# Revit family: IS_iLifeS_E2539_BIM_GB
name_source: partatom
category: Plumbing Fixtures
units: mm (PartAtom-declared; Revit-internal decimal feet)

## family parameters
Always vertical = No
Cut with Voids When Loaded = No
OmniClass Number = 23.45.05.14.14
OmniClass Title = Sinks/Lavatories
Part Type = Normal
Room Calculation Point = No
Round Connector Dimension = Use Diameter
Shared = No
Work Plane-Based = No

## types (1)
- E253901 - i.life S pedestal - White
    Accessories = https://www.idealstandard.co.uk
    AreaUnits = millimetres
    AssetType = Fixed
    BIMObjectName = IS_IdealStandard_Pedestal washbasins_i.lifeS_E2539
    BIMobject category = Wash Basins
    BIMobject category code = wash-basins
    BIMobject main category = Sanitary
    BIMobject main category code = sanitary
    BarCode = 5017830556251
    Brand = Ideal Standard
    Brand url = http://www.idealstandard.co.uk
    Category = Sanitary
    Color = White
    ConnectionType = Plumbing
    Cost = 0 $
    CurrencyUnit = £
    CurrentRevision = 1
    Date of publishing = 27/05/2022
    Description = Ideal Standard i.life S pedestal for hwb i.life S 45x25, white, in carton box, UK pallet
    DurationUnit = Years
    Edition number = 1
    ElementType = Fixed
    ExpectedLife = 99
    Features = pedestal for hwb i.life S 45x25, white, in carton box, UK pallet
    Finish = White
    GTIN code = https://5017830556251
    Help = https://www.idealstandard.co.uk
    IFC Classification = Sanitary Terminal
    Installation instructions = https://www.idealstandard.co.uk
    InstallationInstructions = https://www.idealstandard.co.uk
    IsAutomaticFlush = No
    LinearUnits = Millimetres
    MainColor = White
    MaintenanceInformation = https://www.idealstandard.co.uk
    Manufacturer = Ideal Standard
    Manufacturer name = Ideal Standard
    ManufacturerURL = https://www.idealstandard.co.uk
    Material = Finefireclay
    Material main = Finefireclay
    Model = E253901
    ModelNumber = E253901
    ModelReference = i.life S pedestal
    NBS Reference Code = 45-35-70/365
    NBS Reference Description = Pedestal wash basins
    Name = Pedestal washbasins_i.lifeS_E2539_IdealStandard
    NettWeight = 7.02
    NominalDepth = 158 mm
    NominalHeight = 690 mm  [stored 2.26378 ft]
    NominalLength = 158 mm
    NominalWidth = 167 mm  [stored 0.5479 ft]
    OmniClass Code = 23-21 25 23 15
    OmniClass Description = Pedestals
    PredefinedType = Sanitary
    Product Guid = e0bfb649-9b4f-4173-b1d8-f4b82051926a
    Product SKU = E2539
    Product certification = https://www.idealstandard.co.uk
    Product data url = https://bimobject.com
    Product family = I.life S
    Product group = Sanitary: Pedestals
    Product name = i.life S pedestal
    Product url = https://www.idealstandard.co.uk
    ProductInformation = https://www.idealstandard.co.uk
    QR code = http://bimobject.com
    ReplacementCost = 0
    Shape = Sculpture
    Size = 167 x 158 x 690 mm
    Space = Internal
    SpareParts = https://www.idealstandard.co.uk
    Technical description = https://www.idealstandard.co.uk
    UNSPSC Code = 301815
    URL = https://www.idealstandard.co.uk
    Uniclass 2015 Code = Pr_40_20_96_63
    Uniclass 2015 Name = Pedestal washbasins
    Uniclass2015Code = Pr_40_20_96_63
    Uniclass2015Title = Pedestal washbasins
    Uniclass2015Version = v.25
    Version = 1
    VolumeUnits = Litres
    WRASURL = https://www.wrasapprovals.co.uk
    WarrantyDescription = manufacturer warranty
    WarrantyDurationUnit = years
    Youtube clip = https://www.youtube.com

note: [stored X ft] marks values corroborated as IEEE doubles in the binary element streams (Revit-internal decimal feet)

## geometry (parser evidence)
native form markers: Sweep x2
no freeform markers — native parametric forms only
